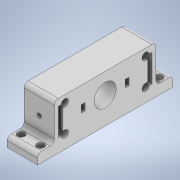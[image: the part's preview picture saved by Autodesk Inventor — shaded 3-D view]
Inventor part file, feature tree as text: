
AUTODESK INVENTOR PART (.ipt)
format: ipt  version: 2020 (Build 240168000, 168)  size: 279,040 bytes
history: native  units: mm
features: extrude x7, sketch x3, other x1, mirror x1, projected_geometry x1
ambient origin geometry x8: Origin, YZ Plane, XZ Plane, XY Plane, X Axis, Y Axis, Z Axis, Center Point
bodies: Body1 (feature_tree)
feature tree (13):
  other  "Bryła1"
  extrude  "Wyciągnięcie proste1"  Depth=33.0mm
  extrude  "Wyciągnięcie proste4"  Depth=10.5mm
  extrude  "Wyciągnięcie proste7"  Depth=40.0mm
  sketch  "Szkic2"
  extrude  "Wyciągnięcie proste5"  Depth=60.0mm
  extrude  "Wyciągnięcie proste6"  Depth=6.0mm
  extrude  "Wyciągnięcie proste9"  Depth=3.5mm
  extrude  "Wyciągnięcie proste10"  TaperAngle=150.0deg  [1 undecoded]
  mirror  "Odbij3"
  sketch  "Szkic3"
  projected_geometry  "Pętla rzutowana1"
  sketch  "Szkic4"
note: 1 required parameter value undecoded (feature->parameter linkage not recoverable at this tier; creation-order binding heuristic only, values carry confidence <= 0.55)
